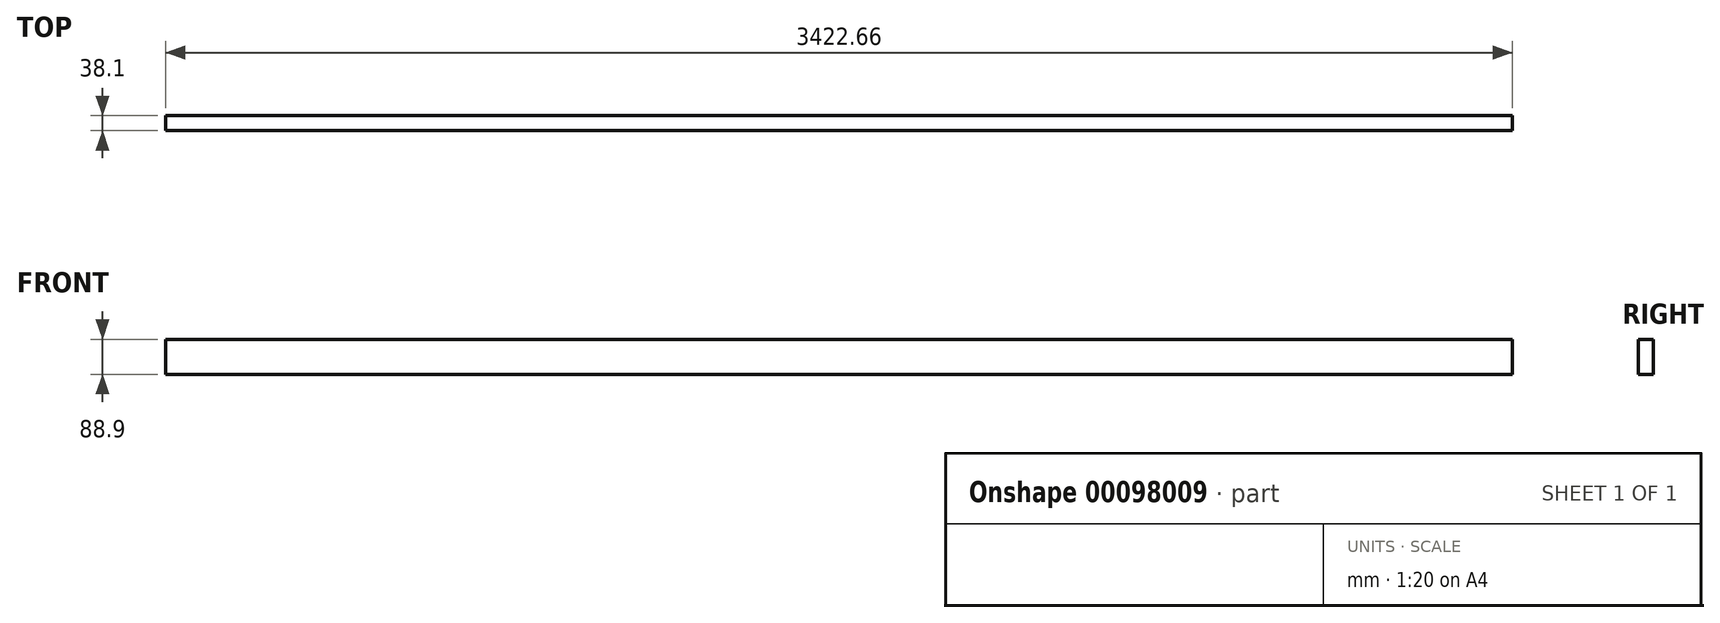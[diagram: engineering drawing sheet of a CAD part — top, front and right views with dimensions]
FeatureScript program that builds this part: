
annotation { "Feature Type Name" : "Feature", "Feature Type Description" : "" }
export const myFeature = defineFeature(function(context is Context, id is Id, definition is map)
    precondition{}
    {
        {
            var Q0;
            Q0=qCreatedBy(makeId("Front.planeOp"),FACE);
            var sketch = newSketch(context, id + "F0", { "sketchPlane" : qUnion([Q0])});
            skLineSegment(sketch, "E0.bottom", {"start": v(1711.33, 44.45) * mm, "end": v(-1711.33, 44.45) * mm});
            skLineSegment(sketch, "E0.top", {"start": v(1711.33, -44.45) * mm, "end": v(-1711.33, -44.45) * mm});
            skLineSegment(sketch, "E0.left", {"start": v(1711.33, 44.45) * mm, "end": v(1711.33, -44.45) * mm});
            skLineSegment(sketch, "E0.right", {"start": v(-1711.33, 44.45) * mm, "end": v(-1711.33, -44.45) * mm});
            skPoint(sketch, "E0.middle", {"position": v(0, 0) * mm});
            skSolve(sketch);
        }
        {
            var Q0;
            Q0=makeQuery(id+"F0.imprint","IMPRINT",FACE,{"disambiguationData":[TD([[makeQuery(id+"F0.imprint","IMPRINT",EDGE,{"derivedFrom":sQuery(id+"F0.wireOp",EDGE,"E0.bottom")}),1.0]])]});
            extrude(context, id + "F1", {"entities" : qUnion([Q0]), "depth" : 38.1 * mm});
        }
    });
